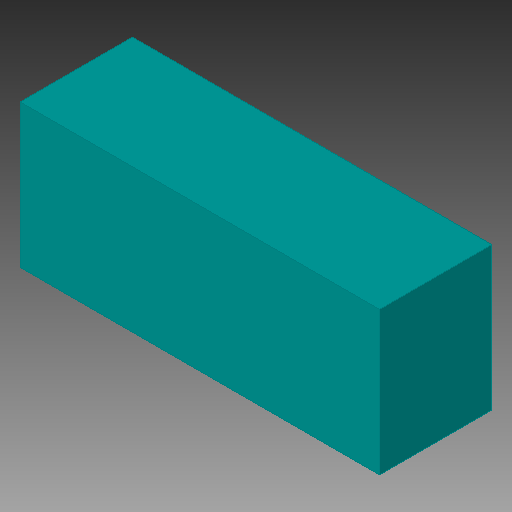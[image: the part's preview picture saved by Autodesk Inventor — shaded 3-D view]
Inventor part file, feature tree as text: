
AUTODESK INVENTOR PART (.ipt)
format: ipt  version: 2018 (Build 220112000, 112)  size: 80,384 bytes
history: native  units: in
note: dims shown in document units (in); Inventor stores cm internally (conversion verified against a paired STEP export)
features: other x1, extrude x1
ambient origin geometry x8: Origin, YZ Plane, XZ Plane, XY Plane, X Axis, Y Axis, Z Axis, Center Point
bodies: Solid1 (feature_tree)
feature tree (2):
  other  "A_3216-18R, A_3216-18R_14"
  extrude  "Extrusion1"  Depth=0.0394in TaperAngle=0.0deg
